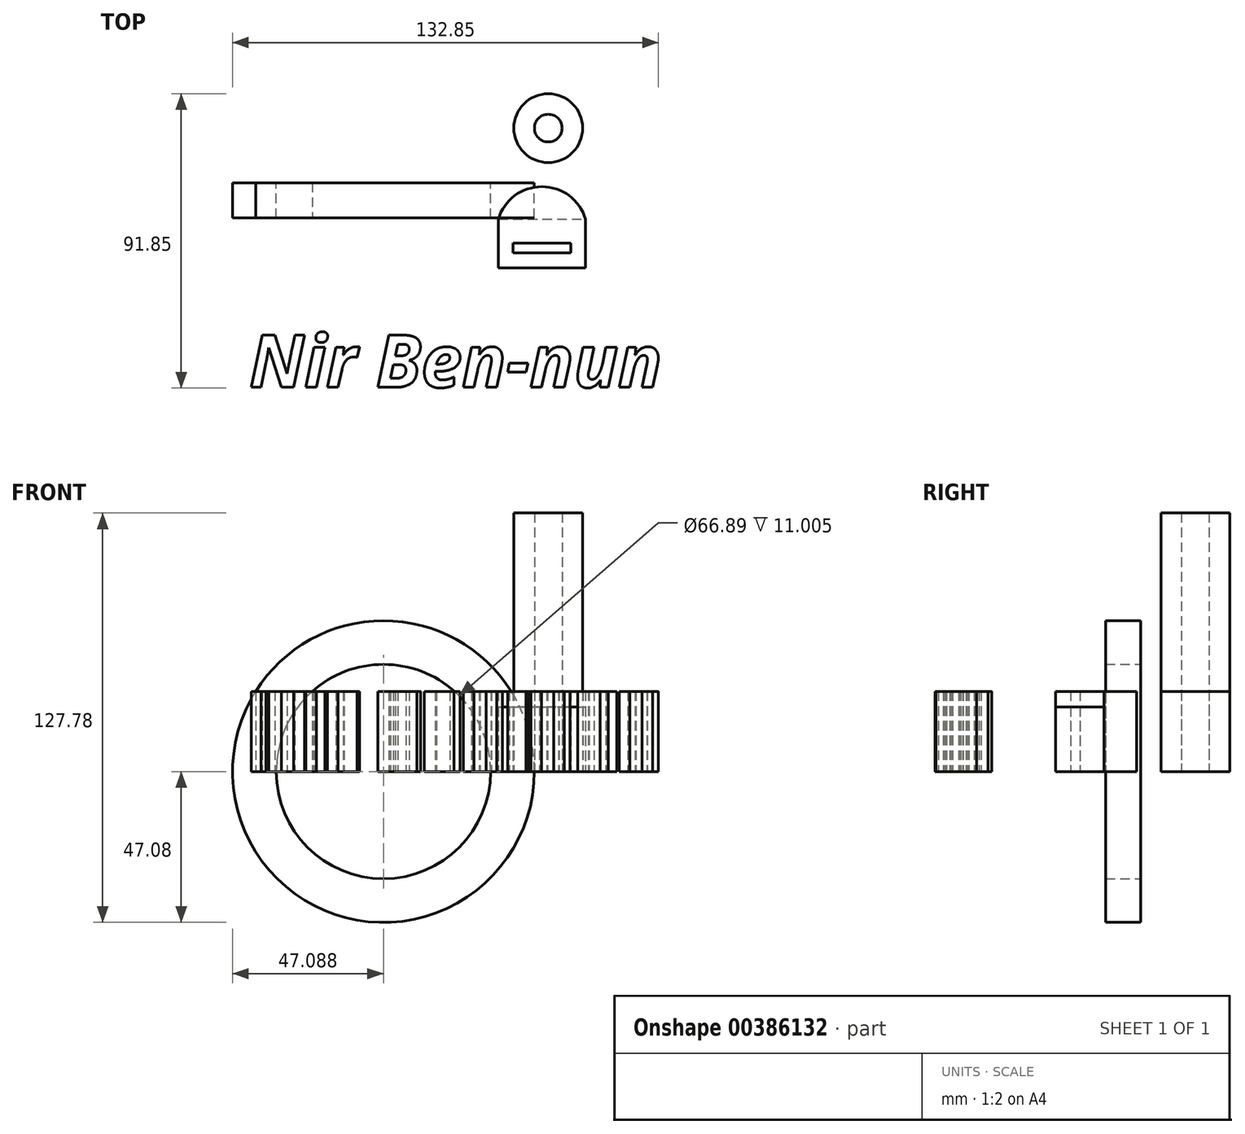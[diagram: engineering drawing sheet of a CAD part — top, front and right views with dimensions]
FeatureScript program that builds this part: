
annotation { "Feature Type Name" : "Feature", "Feature Type Description" : "" }
export const myFeature = defineFeature(function(context is Context, id is Id, definition is map)
    precondition{}
    {
        {
            var Q0;
            Q0=qCreatedBy(makeId("Top.planeOp"),FACE);
            var sketch = newSketch(context, id + "F0", { "sketchPlane" : qUnion([Q0])});
            skLineSegment(sketch, "E0.bottom", {"start": v(14.2, 20.08) * mm, "end": v(41.47, 20.08) * mm});
            skLineSegment(sketch, "E0.top", {"start": v(14.2, 4.93) * mm, "end": v(41.47, 4.93) * mm});
            skLineSegment(sketch, "E0.left", {"start": v(14.2, 20.08) * mm, "end": v(14.2, 4.93) * mm});
            skLineSegment(sketch, "E0.right", {"start": v(41.47, 20.08) * mm, "end": v(41.47, 4.93) * mm});
            skCircle(sketch, "E1", {"center": v(29.8, 48.52) * mm, "radius": 10.73 * mm});
            skCircle(sketch, "E2", {"center": v(29.8, 48.52) * mm, "radius": 4.32 * mm});
            skLineSegment(sketch, "E3", {"start": v(-21.62, 34.34) * mm, "end": v(-21.62, 13.67) * mm, "construction": true});
            skArc(sketch, "E4", {"start": v(41.47, 20.08) * mm, "mid": v(27.83, 30.24) * mm, "end": v(14.2, 20.08) * mm});
            skLineSegment(sketch, "E5.bottom", {"start": v(27.83, 12.6) * mm, "end": v(18.83, 12.6) * mm});
            skLineSegment(sketch, "E5.top", {"start": v(27.83, 9.57) * mm, "end": v(18.83, 9.57) * mm});
            skLineSegment(sketch, "E5.left", {"start": v(27.83, 12.6) * mm, "end": v(27.83, 9.57) * mm});
            skLineSegment(sketch, "E5.right", {"start": v(18.83, 12.6) * mm, "end": v(18.83, 9.57) * mm});
            skPoint(sketch, "E6.oppositeSnap0", {"position": v(23.33, 9.57) * mm});
            skLineSegment(sketch, "E6.bottom", {"start": v(27.83, 12.6) * mm, "end": v(36.83, 12.6) * mm});
            skLineSegment(sketch, "E6.top", {"start": v(27.83, 9.57) * mm, "end": v(36.83, 9.57) * mm});
            skLineSegment(sketch, "E6.right", {"start": v(36.83, 12.6) * mm, "end": v(36.83, 9.57) * mm});
            skText(sketch, "E7", { "text": "Nir Ben-nun", "fontName": "OpenSans-BoldItalic.ttf"});
            skLineSegment(sketch, "E8.bottom", {"start": v(-61.52, 31.48) * mm, "end": v(-43.84, 31.48) * mm});
            skLineSegment(sketch, "E8.top", {"start": v(-61.52, 20.48) * mm, "end": v(-43.84, 20.48) * mm});
            skLineSegment(sketch, "E8.left", {"start": v(-61.52, 31.48) * mm, "end": v(-61.52, 20.48) * mm});
            skLineSegment(sketch, "E8.right", {"start": v(-43.84, 31.48) * mm, "end": v(-43.84, 20.48) * mm});
            const initialGuessF0  = {"E7": [-0.0635, -0.03238, 1, 0, 0.01642]};
            skSetInitialGuess(sketch, initialGuessF0);
            skSolve(sketch);
        }
        {
            var Q0;
            Q0=makeQuery(id+"F0.imprint","IMPRINT",FACE,{"disambiguationData":[TD([[makeQuery(id+"F0.imprint","IMPRINT",EDGE,{"derivedFrom":sQuery(id+"F0.wireOp",EDGE,"E0.bottom")}),-1.0]])]});
            extrude(context, id + "F1", {"entities" : qUnion([Q0]), "depth" : 20.1 * mm});
        }
        {
            var Q0;
            Q0=makeQuery(id+"F0.imprint","IMPRINT",FACE,{"disambiguationData":[TD([[makeQuery(id+"F0.imprint","IMPRINT",EDGE,{"derivedFrom":sQuery(id+"F0.wireOp",EDGE,"E1")}),1.0]])]});
            extrude(context, id + "F2", {"entities" : qUnion([Q0]), "depth" : 80.7 * mm});
        }
        {
            var Q0;
            Q0=makeQuery(id+"F0.imprint","IMPRINT",FACE,{"disambiguationData":[TD([[makeQuery(id+"F0.imprint","IMPRINT",EDGE,{"derivedFrom":sQuery(id+"F0.wireOp",EDGE,"E0.bottom")}),1.0]])]});
            var Q1;
            Q1=sQuery(id+"F0.wireOp",EDGE,"E4");
            extrude(context, id + "F3", {"entities" : qUnion([Q0]), "bodyType" : ToolBodyType.SURFACE, "surfaceEntities" : qUnion([Q1]), "depth" : 19.6 * mm});
        }
        {
            var Q0;
            Q0=makeQuery(id+"F0.imprint","IMPRINT",FACE,{"disambiguationData":[TD([[makeQuery(id+"F0.imprint","IMPRINT",EDGE,{"derivedFrom":sQuery(id+"F0.wireOp",EDGE,"E5.bottom")}),1.0]])]});
            var Q1;
            Q1=makeQuery(id+"F0.imprint","IMPRINT",FACE,{"disambiguationData":[TD([[makeQuery(id+"F0.imprint","IMPRINT",EDGE,{"derivedFrom":sQuery(id+"F0.wireOp",EDGE,"E6.bottom")}),-1.0]])]});
            extrude(context, id + "F4", {"entities" : qUnion([Q0, Q1]), "operationType" : NewBodyOperationType.REMOVE, "oppositeDirection" : true, "depth" : 25 * mm});
        }
        {
            var Q0;
            Q0 = qSketchRegion(id + "F0", true);
            extrude(context, id + "F5", {"entities" : qUnion([Q0]), "depth" : 25 * mm});
        }
        {
            var Q0;
            Q0=makeQuery(id+"F5.opExtrude","CAP_FACE",FACE,{"disambiguationData":[OSD([sQuery(id+"F0.wireOp",EDGE,"E8.bottom"),sQuery(id+"F0.wireOp",EDGE,"E8.top"),sQuery(id+"F0.wireOp",EDGE,"E8.left"),sQuery(id+"F0.wireOp",EDGE,"E8.right")])],"isStart":false});
            var Q1;
            Q1=sQuery(id+"F0.wireOp",EDGE,"E3");
            revolve(context, id + "F6", {"entities" : qUnion([Q0]), "axis" : qUnion([Q1]), "revolveType" : RevolveType.FULL});
        }
    });
